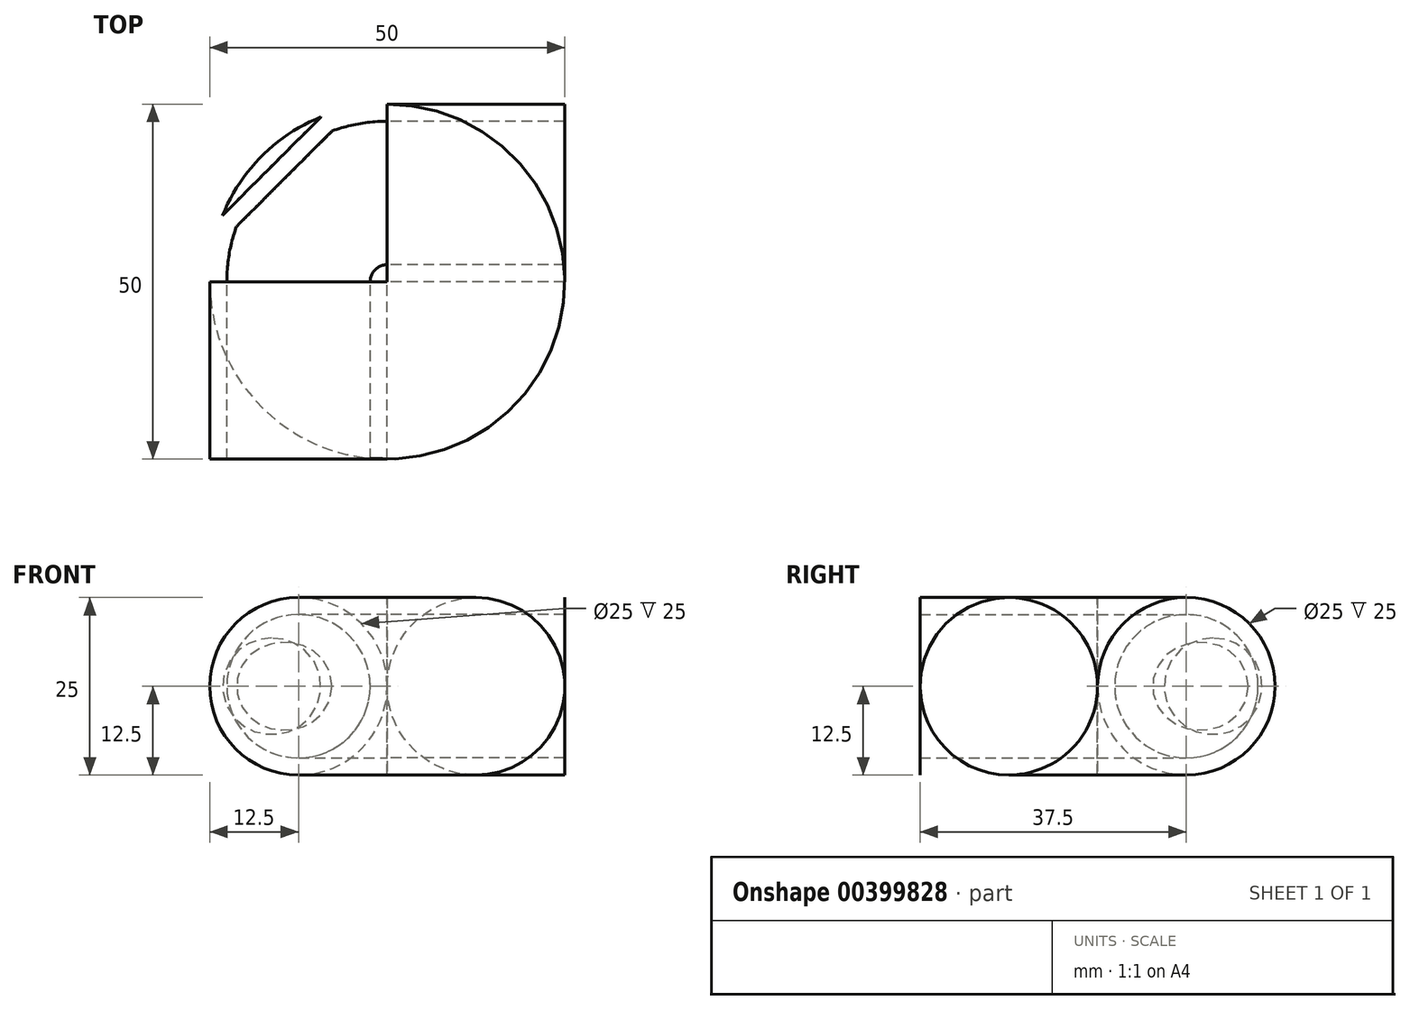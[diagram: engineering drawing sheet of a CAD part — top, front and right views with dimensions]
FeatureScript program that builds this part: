
annotation { "Feature Type Name" : "Feature", "Feature Type Description" : "" }
export const myFeature = defineFeature(function(context is Context, id is Id, definition is map)
    precondition{}
    {
        {
            var Q0;
            Q0=qCreatedBy(makeId("Front.planeOp"),FACE);
            var sketch = newSketch(context, id + "F0", { "sketchPlane" : qUnion([Q0])});
            skCircle(sketch, "E0", {"center": v(0, 0) * mm, "radius": 10.1 * mm});
            skCircle(sketch, "E1", {"center": v(0, 0) * mm, "radius": 12.5 * mm});
            skSolve(sketch);
        }
        {
            var Q0;
            Q0=qCreatedBy(makeId("Top.planeOp"),FACE);
            var sketch = newSketch(context, id + "F1", { "sketchPlane" : qUnion([Q0])});
            skLineSegment(sketch, "E2", {"start": v(12.5, 0) * mm, "end": v(12.5, 8.86) * mm, "construction": true});
            skArc(sketch, "E3", {"start": v(0, 0) * mm, "mid": v(3.66, 8.84) * mm, "end": v(12.5, 12.5) * mm});
            skSolve(sketch);
        }
        {
            var Q0;
            Q0=makeQuery(id+"F0.imprint","IMPRINT",FACE,{"disambiguationData":[TD([[makeQuery(id+"F0.imprint","IMPRINT",EDGE,{"derivedFrom":sQuery(id+"F0.wireOp",EDGE,"E0")}),-1.0]])]});
            var Q1;
            Q1=sQuery(id+"F1.wireOp",EDGE,"E3");
            sweep(context, id + "F2", {"profiles" : qUnion([Q0]), "path" : qUnion([Q1])});
        }
        {
            var Q0;
            Q0=makeQuery(id+"F2.opSweep","CAP_FACE",FACE,{"disambiguationData":[OSD([sQuery(id+"F0.wireOp",EDGE,"E0"),sQuery(id+"F0.wireOp",EDGE,"E1"),sQuery(id+"F1.wireOp",VERTEX,"E3.start")])],"isStart":true});
            var sketch = newSketch(context, id + "F3", { "sketchPlane" : qUnion([Q0])});
            skCircle(sketch, "E4", {"center": v(0, 0) * mm, "radius": 10.1 * mm});
            skCircle(sketch, "E5", {"center": v(0, 0) * mm, "radius": 12.5 * mm});
            skSolve(sketch);
        }
        {
            var Q0;
            Q0 = qSketchRegion(id + "F3", true);
            extrude(context, id + "F4", {"entities" : qUnion([Q0]), "operationType" : NewBodyOperationType.ADD, "depth" : 25 * mm});
        }
        {
            var Q0;
            Q0=makeQuery(id+"F2.opSweep","CAP_FACE",FACE,{"disambiguationData":[OSD([sQuery(id+"F0.wireOp",EDGE,"E0"),sQuery(id+"F0.wireOp",EDGE,"E1"),sQuery(id+"F1.wireOp",VERTEX,"E3.end")])],"isStart":false});
            var sketch = newSketch(context, id + "F5", { "sketchPlane" : qUnion([Q0])});
            skCircle(sketch, "E6", {"center": v(12.5, 0) * mm, "radius": 10.1 * mm});
            skCircle(sketch, "E7", {"center": v(12.5, 0) * mm, "radius": 12.5 * mm});
            skSolve(sketch);
        }
        {
            var Q0;
            Q0 = qSketchRegion(id + "F5", true);
            extrude(context, id + "F6", {"entities" : qUnion([Q0]), "operationType" : NewBodyOperationType.ADD, "depth" : 25 * mm});
        }
        {
            var Q0;
            Q0=makeQuery(id+"F2.opSweep","SWEPT_FACE",FACE,{"disambiguationData":[OSD([sQuery(id+"F0.wireOp",EDGE,"E1"),sQuery(id+"F1.wireOp",EDGE,"E3")])]});
            cPlane(context, id + "F7", {"entities" : qUnion([Q0]), "cplaneType" : CPlaneType.LINE_ANGLE, "offset" : 25 * mm, "angle" : 45 * degree, "width" : 150 * mm, "height" : 150 * mm});
        }
        {
            var Q0;
            Q0=qCreatedBy(id+"F7.planeOp",FACE);
            cPlane(context, id + "F8", {"entities" : qUnion([Q0]), "cplaneType" : CPlaneType.OFFSET, "offset" : 25 * mm, "width" : 150 * mm, "height" : 150 * mm});
        }
        {
            var Q0;
            Q0=qCreatedBy(id+"F8.planeOp",FACE);
            var sketch = newSketch(context, id + "F9", { "sketchPlane" : qUnion([Q0])});
            skLineSegment(sketch, "E8.bottom", {"start": v(11.16, 10) * mm, "end": v(-28.84, 10) * mm});
            skLineSegment(sketch, "E8.top", {"start": v(11.16, -10) * mm, "end": v(-28.84, -10) * mm});
            skLineSegment(sketch, "E8.left", {"start": v(11.16, 10) * mm, "end": v(11.16, -10) * mm});
            skLineSegment(sketch, "E8.right", {"start": v(-28.84, 10) * mm, "end": v(-28.84, -10) * mm});
            skPoint(sketch, "E8.middle", {"position": v(-8.84, 0) * mm});
            skSolve(sketch);
        }
        {
            var Q0;
            Q0 = qSketchRegion(id + "F9", true);
            extrude(context, id + "F10", {"entities" : qUnion([Q0]), "operationType" : NewBodyOperationType.REMOVE, "oppositeDirection" : true, "depth" : 2 * mm});
        }
        {
            var Q0;
            Q0=qCreatedBy(id+"F8.planeOp",FACE);
            cPlane(context, id + "F11", {"entities" : qUnion([Q0]), "cplaneType" : CPlaneType.OFFSET, "offset" : 4.5 * mm, "oppositeDirection" : true, "width" : 150 * mm, "height" : 150 * mm});
        }
        {
            var Q0;
            Q0=qCreatedBy(id+"F11.planeOp",FACE);
            var sketch = newSketch(context, id + "F12", { "sketchPlane" : qUnion([Q0])});
            skEllipse(sketch, "E9", {"center": v(-8.91, 0) * mm, "majorRadius": 7.39 * mm, "minorRadius": 11.31 * mm, "majorAxis": v(0, 1)});
            skSolve(sketch);
        }
        {
            var Q0;
            Q0 = qSketchRegion(id + "F12", true);
            var Q1;
            Q1=makeQuery(id+"F2.opSweep","SWEPT_FACE",FACE,{"disambiguationData":[OSD([sQuery(id+"F0.wireOp",EDGE,"E0"),sQuery(id+"F1.wireOp",EDGE,"E3")])]});
            extrude(context, id + "F13", {"entities" : qUnion([Q0]), "operationType" : NewBodyOperationType.ADD, "endBound" : BoundingType.UP_TO_SURFACE, "endBoundEntityFace" : qUnion([Q1]), "depth" : 25 * mm});
        }
    });
